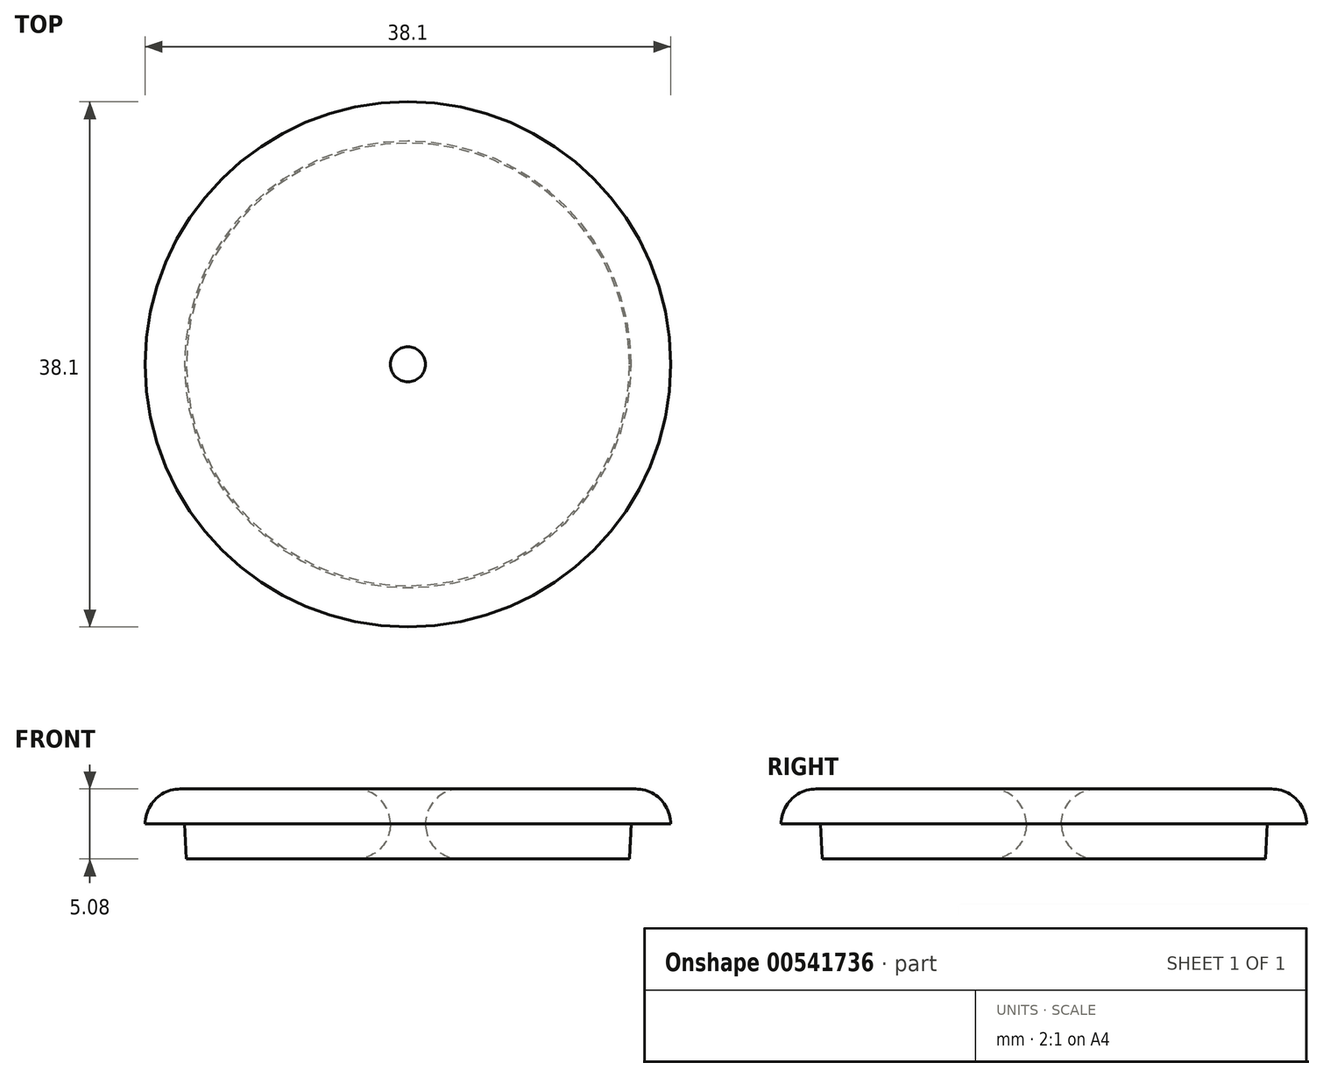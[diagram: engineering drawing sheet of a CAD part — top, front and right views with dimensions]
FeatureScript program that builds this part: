
annotation { "Feature Type Name" : "Feature", "Feature Type Description" : "" }
export const myFeature = defineFeature(function(context is Context, id is Id, definition is map)
    precondition{}
    {
        {
            var Q0;
            Q0=qCreatedBy(makeId("Top.planeOp"),FACE);
            var sketch = newSketch(context, id + "F0", { "sketchPlane" : qUnion([Q0])});
            skCircle(sketch, "E0", {"center": v(0, 0) * mm, "radius": 16.2 * mm});
            skCircle(sketch, "E1", {"center": v(0, 0) * mm, "radius": 19.05 * mm});
            skCircle(sketch, "E2", {"center": v(0, 0) * mm, "radius": 1.27 * mm});
            skSolve(sketch);
        }
        {
            var Q0;
            Q0=makeQuery(id+"F0.imprint","IMPRINT",FACE,{"disambiguationData":[TD([[makeQuery(id+"F0.imprint","IMPRINT",EDGE,{"derivedFrom":sQuery(id+"F0.wireOp",EDGE,"E0")}),-1.0]])]});
            var Q1;
            Q1=makeQuery(id+"F0.imprint","IMPRINT",FACE,{"disambiguationData":[TD([[makeQuery(id+"F0.imprint","IMPRINT",EDGE,{"derivedFrom":sQuery(id+"F0.wireOp",EDGE,"E0")}),1.0]])]});
            var Q2;
            Q2=sQuery(id+"F0.wireOp",EDGE,"E1");
            extrude(context, id + "F1", {"entities" : qUnion([Q0, Q1]), "surfaceEntities" : qUnion([Q2]), "depth" : 2.54 * mm, "offsetDistance" : 25.4 * mm});
        }
        {
            var Q0;
            Q0=makeQuery(id+"F0.imprint","IMPRINT",FACE,{"disambiguationData":[TD([[makeQuery(id+"F0.imprint","IMPRINT",EDGE,{"derivedFrom":sQuery(id+"F0.wireOp",EDGE,"E0")}),1.0]])]});
            var Q1;
            Q1=sQuery(id+"F0.wireOp",EDGE,"E0");
            extrude(context, id + "F2", {"entities" : qUnion([Q0]), "surfaceEntities" : qUnion([Q1]), "oppositeDirection" : true, "depth" : 2.54 * mm, "offsetDistance" : 25.4 * mm, "hasDraft" : true, "draftAngle" : 3 * degree, "draftPullDirection" : true});
        }
        {
            var Q0;
            Q0=makeQuery(id+"F1.opExtrude","CAP_EDGE",EDGE,{"disambiguationData":[OSD([sQuery(id+"F0.wireOp",EDGE,"E1")])],"isStart":false});
            fillet(context, id + "F3", {"entities" : qUnion([Q0]), "radius" : 2.54 * mm, "tangentPropagation" : true, "allowEdgeOverflow" : false});
        }
        {
            var Q0;
            Q0=makeQuery(id+"F1.opExtrude","CAP_EDGE",EDGE,{"disambiguationData":[OSD([sQuery(id+"F0.wireOp",EDGE,"E2")])],"isStart":false});
            var Q1;
            Q1=makeQuery(id+"F2.opExtrude","CAP_EDGE",EDGE,{"disambiguationData":[OSD([sQuery(id+"F0.wireOp",EDGE,"E2")])],"isStart":false});
            fillet(context, id + "F4", {"entities" : qUnion([Q0, Q1]), "radius" : 2.54 * mm, "tangentPropagation" : true, "allowEdgeOverflow" : false});
        }
    });
